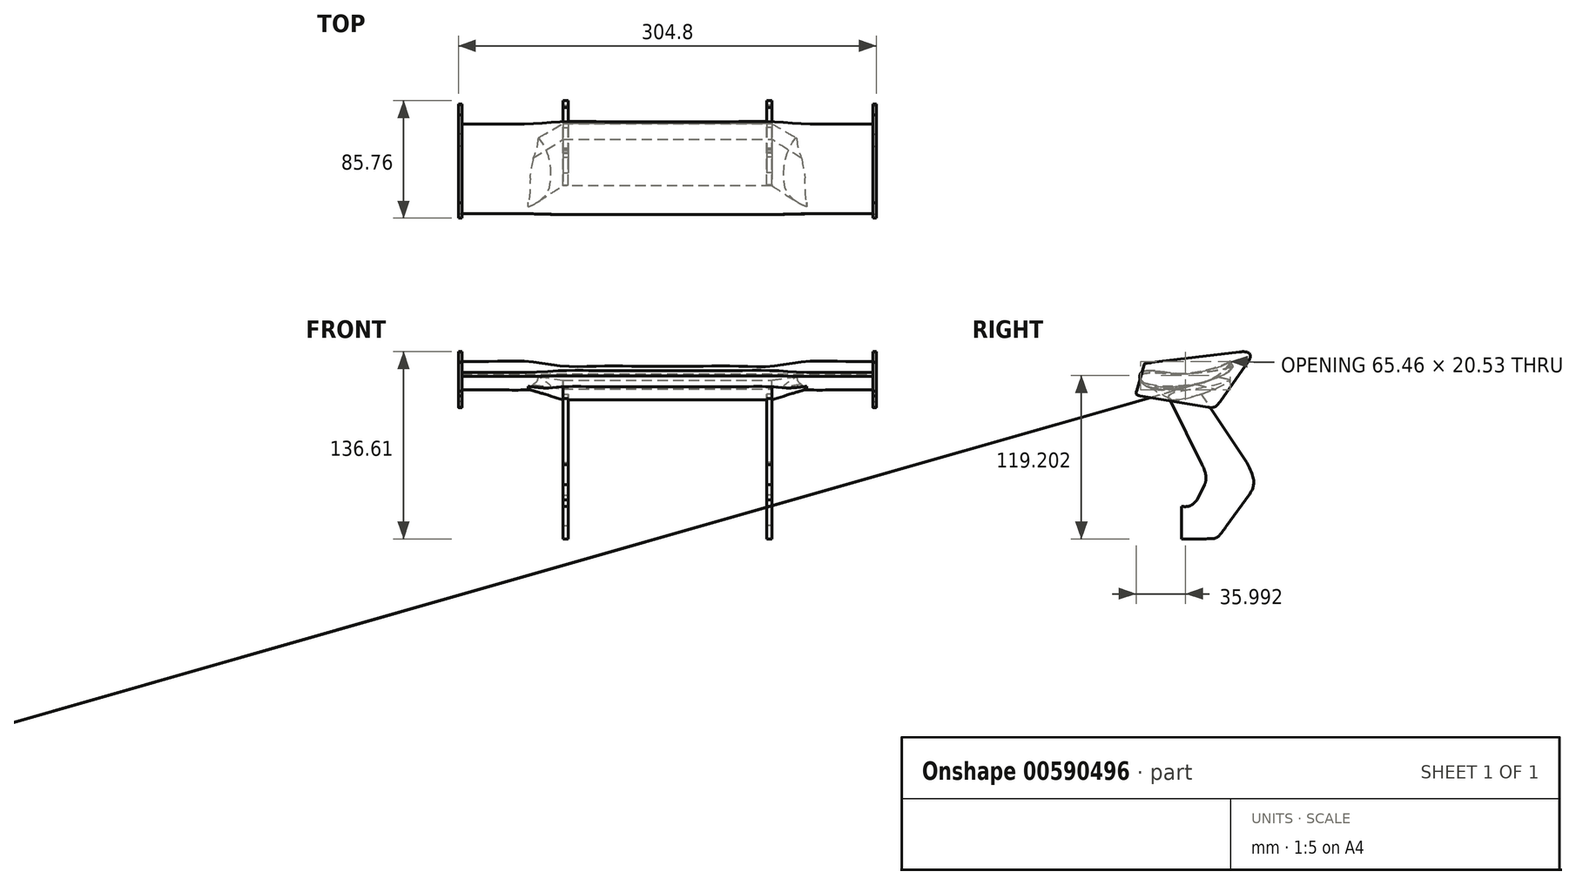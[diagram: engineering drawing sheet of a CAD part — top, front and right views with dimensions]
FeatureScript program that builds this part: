
annotation { "Feature Type Name" : "Feature", "Feature Type Description" : "" }
export const myFeature = defineFeature(function(context is Context, id is Id, definition is map)
    precondition{}
    {
        {
            var Q0;
            Q0=qCreatedBy(makeId("Right.planeOp"),FACE);
            cPlane(context, id + "F0", {"entities" : qUnion([Q0]), "cplaneType" : CPlaneType.OFFSET, "offset" : 25.4 * mm, "width" : 152.4 * mm, "height" : 152.4 * mm});
        }
        {
            var Q0;
            Q0=qCreatedBy(id+"F0.planeOp",FACE);
            cPlane(context, id + "F1", {"entities" : qUnion([Q0]), "cplaneType" : CPlaneType.OFFSET, "offset" : 25.4 * mm, "width" : 152.4 * mm, "height" : 152.4 * mm});
        }
        {
            var Q0;
            Q0=qCreatedBy(id+"F1.planeOp",FACE);
            cPlane(context, id + "F2", {"entities" : qUnion([Q0]), "cplaneType" : CPlaneType.OFFSET, "offset" : 25.4 * mm, "width" : 152.4 * mm, "height" : 152.4 * mm});
        }
        {
            var Q0;
            Q0=qCreatedBy(id+"F2.planeOp",FACE);
            cPlane(context, id + "F3", {"entities" : qUnion([Q0]), "cplaneType" : CPlaneType.OFFSET, "offset" : 25.4 * mm, "width" : 152.4 * mm, "height" : 152.4 * mm});
        }
        {
            var Q0;
            Q0=qCreatedBy(id+"F3.planeOp",FACE);
            cPlane(context, id + "F4", {"entities" : qUnion([Q0]), "cplaneType" : CPlaneType.OFFSET, "offset" : 25.4 * mm, "width" : 152.4 * mm, "height" : 152.4 * mm});
        }
        {
            var Q0;
            Q0=qCreatedBy(id+"F4.planeOp",FACE);
            cPlane(context, id + "F5", {"entities" : qUnion([Q0]), "cplaneType" : CPlaneType.OFFSET, "offset" : 25.4 * mm, "width" : 152.4 * mm, "height" : 152.4 * mm});
        }
        {
            var Q0;
            Q0=qCreatedBy(id+"F0.planeOp",FACE);
            var sketch = newSketch(context, id + "F6", { "sketchPlane" : qUnion([Q0])});
            skFitSpline(sketch, "E0", {"points": [v(-32.84, 0.21) * mm, v(-26.14, -7.71) * mm, v(-13.87, -9.4) * mm, v(5.28, -6.18) * mm, v(19.7, -1.36) * mm, v(29.56, 6.15) * mm, v(32.6, 11.17) * mm], "startDerivative": vector(-17.98, -81.92) * mm, "endDerivative": vector(4.77, 35.61) * mm});
            skFitSpline(sketch, "E1", {"points": [v(32.6, 11.17) * mm, v(14.13, 4.43) * mm, v(-8.08, 1.98) * mm, v(-25.23, 3.12) * mm, v(-32.84, 0.21) * mm], "startDerivative": vector(-30.77, -27.63) * mm, "endDerivative": vector(-5.16, -33) * mm});
            skSolve(sketch);
        }
        {
            var Q0;
            Q0=qCreatedBy(makeId("Right.planeOp"),FACE);
            var sketch = newSketch(context, id + "F7", { "sketchPlane" : qUnion([Q0])});
            skFitSpline(sketch, "E2", {"points": [v(-32.84, 0.21) * mm, v(-26.14, -7.71) * mm, v(-13.87, -9.4) * mm, v(5.28, -6.18) * mm, v(19.7, -1.36) * mm, v(29.56, 6.15) * mm, v(32.6, 11.17) * mm], "startDerivative": vector(-17.98, -81.92) * mm, "endDerivative": vector(4.77, 35.61) * mm});
            skFitSpline(sketch, "E3", {"points": [v(32.6, 11.17) * mm, v(14.13, 4.43) * mm, v(-8.08, 1.98) * mm, v(-25.23, 3.12) * mm, v(-32.84, 0.21) * mm], "startDerivative": vector(-30.77, -27.63) * mm, "endDerivative": vector(-5.16, -33) * mm});
            skSolve(sketch);
        }
        {
            var Q0;
            Q0=qCreatedBy(makeId("Right.planeOp"),FACE);
            cPlane(context, id + "F8", {"entities" : qUnion([Q0]), "cplaneType" : CPlaneType.OFFSET, "offset" : 25.4 * mm, "oppositeDirection" : true, "width" : 152.4 * mm, "height" : 152.4 * mm});
        }
        {
            var Q0;
            Q0=qCreatedBy(id+"F8.planeOp",FACE);
            var sketch = newSketch(context, id + "F9", { "sketchPlane" : qUnion([Q0])});
            skFitSpline(sketch, "E4", {"points": [v(-32.84, 0.21) * mm, v(-26.14, -7.71) * mm, v(-13.87, -9.4) * mm, v(5.28, -6.18) * mm, v(19.7, -1.36) * mm, v(29.56, 6.15) * mm, v(32.6, 11.17) * mm], "startDerivative": vector(-17.98, -81.92) * mm, "endDerivative": vector(4.77, 35.61) * mm});
            skFitSpline(sketch, "E5", {"points": [v(32.6, 11.17) * mm, v(14.13, 4.43) * mm, v(-8.08, 1.98) * mm, v(-25.23, 3.12) * mm, v(-32.84, 0.21) * mm], "startDerivative": vector(-30.77, -27.63) * mm, "endDerivative": vector(-5.16, -33) * mm});
            skSolve(sketch);
        }
        {
            var Q0;
            Q0=qCreatedBy(id+"F4.planeOp",FACE);
            var sketch = newSketch(context, id + "F10", { "sketchPlane" : qUnion([Q0])});
            skFitSpline(sketch, "E6", {"points": [v(-33.46, 0.63) * mm, v(-21.57, -6.7) * mm, v(-14.4, -7.32) * mm, v(5.2, -5.74) * mm, v(19.3, -2.02) * mm, v(30.63, 3.33) * mm, v(34.3, 7.73) * mm], "startDerivative": vector(-17.98, -81.92) * mm, "endDerivative": vector(25.2, 44.48) * mm});
            skFitSpline(sketch, "E7", {"points": [v(34.3, 7.73) * mm, v(13.83, 3.16) * mm, v(-8.88, 2.6) * mm, v(-30.7, 4) * mm, v(-33.46, 0.63) * mm], "startDerivative": vector(-40.26, -20.43) * mm, "endDerivative": vector(-5.16, -33) * mm});
            skSolve(sketch);
        }
        {
            var Q0;
            Q0=qCreatedBy(id+"F3.planeOp",FACE);
            var sketch = newSketch(context, id + "F11", { "sketchPlane" : qUnion([Q0])});
            skFitSpline(sketch, "E8", {"points": [v(-33.46, 0.63) * mm, v(-21.57, -6.7) * mm, v(-14.4, -7.32) * mm, v(5.2, -5.74) * mm, v(19.3, -2.02) * mm, v(30.63, 3.33) * mm, v(34.3, 7.73) * mm], "startDerivative": vector(-17.98, -81.92) * mm, "endDerivative": vector(25.2, 44.48) * mm});
            skFitSpline(sketch, "E9", {"points": [v(34.3, 7.73) * mm, v(13.83, 3.16) * mm, v(-8.88, 2.6) * mm, v(-30.7, 4) * mm, v(-33.46, 0.63) * mm], "startDerivative": vector(-40.26, -20.43) * mm, "endDerivative": vector(-5.16, -33) * mm});
            skSolve(sketch);
        }
        {
            var Q0;
            Q0=qCreatedBy(id+"F2.planeOp",FACE);
            var sketch = newSketch(context, id + "F12", { "sketchPlane" : qUnion([Q0])});
            skFitSpline(sketch, "E10", {"points": [v(-33.46, 0.63) * mm, v(-21.57, -6.7) * mm, v(-14.4, -7.32) * mm, v(5.2, -5.74) * mm, v(19.3, -2.02) * mm, v(30.63, 3.33) * mm, v(34.3, 7.73) * mm], "startDerivative": vector(-17.98, -81.92) * mm, "endDerivative": vector(25.2, 44.48) * mm});
            skFitSpline(sketch, "E11", {"points": [v(34.3, 7.73) * mm, v(13.83, 3.16) * mm, v(-8.88, 2.6) * mm, v(-30.7, 4) * mm, v(-33.46, 0.63) * mm], "startDerivative": vector(-40.26, -20.43) * mm, "endDerivative": vector(-5.16, -33) * mm});
            skSolve(sketch);
        }
        {
            var Q0;
            Q0=qCreatedBy(id+"F1.planeOp",FACE);
            var sketch = newSketch(context, id + "F13", { "sketchPlane" : qUnion([Q0])});
            skFitSpline(sketch, "E12", {"points": [v(-33.46, 0.63) * mm, v(-21.57, -6.7) * mm, v(-14.4, -7.32) * mm, v(5.2, -5.74) * mm, v(19.3, -2.02) * mm, v(30.63, 3.33) * mm, v(34.3, 7.73) * mm], "startDerivative": vector(-17.98, -81.92) * mm, "endDerivative": vector(25.2, 44.48) * mm});
            skFitSpline(sketch, "E13", {"points": [v(34.3, 7.73) * mm, v(13.83, 3.16) * mm, v(-8.88, 2.6) * mm, v(-30.7, 4) * mm, v(-33.46, 0.63) * mm], "startDerivative": vector(-40.26, -20.43) * mm, "endDerivative": vector(-5.16, -33) * mm});
            skSolve(sketch);
        }
        {
            var Q0;
            Q0=qCreatedBy(id+"F4.planeOp",FACE);
            var sketch = newSketch(context, id + "F14", { "sketchPlane" : qUnion([Q0])});
            skFitSpline(sketch, "E14", {"points": [v(32.78, -2.46) * mm, v(15.02, -7.23) * mm, v(-1.74, -10.05) * mm, v(-12.15, -13.46) * mm, v(-11.52, -16.01) * mm, v(-4, -16.68) * mm, v(6.68, -14.11) * mm, v(21.31, -8.94) * mm], "startDerivative": vector(-110.1, -36.5) * mm, "endDerivative": vector(216.78, 82.36) * mm});
            skFitSpline(sketch, "E15", {"points": [v(21.31, -8.94) * mm, v(32.78, -2.46) * mm], "startDerivative": vector(9.03, 3.91) * mm, "endDerivative": vector(0, 2.47) * mm});
            skSolve(sketch);
        }
        {
            var Q0;
            Q0=makeQuery(id+"F14.imprint","IMPRINT",FACE,{"disambiguationData":[TD([[makeQuery(id+"F14.imprint","IMPRINT",EDGE,{"derivedFrom":sQuery(id+"F14.wireOp",EDGE,"E14")}),1.0]])]});
            extrude(context, id + "F15", {"entities" : qUnion([Q0]), "oppositeDirection" : true, "depth" : 76.2 * mm, "offsetDistance" : 25.4 * mm});
        }
        {
            var Q0;
            Q0=qCreatedBy(id+"F0.planeOp",FACE);
            var sketch = newSketch(context, id + "F16", { "sketchPlane" : qUnion([Q0])});
            skFitSpline(sketch, "E16", {"points": [v(18.16, 1.16) * mm, v(-2.89, -2.52) * mm, v(-22.26, -3.13) * mm, v(-28.7, -4.47) * mm, v(-28.03, -6.81) * mm, v(-15.83, -9.03) * mm, v(-8.45, -8.29) * mm, v(5.36, -5) * mm], "startDerivative": vector(-110.1, -36.5) * mm, "endDerivative": vector(240, 68.21) * mm});
            skFitSpline(sketch, "E17", {"points": [v(5.36, -5) * mm, v(18.16, 1.16) * mm], "startDerivative": vector(9.03, 3.91) * mm, "endDerivative": vector(0, 2.47) * mm});
            skSolve(sketch);
        }
        {
            var Q1;
            Q1 = qSketchRegion(id + "F16", true);
            var Q2;
            Q2=makeQuery(id+"F15.opExtrude","CAP_FACE",FACE,{"disambiguationData":[OSD([sQuery(id+"F14.wireOp",EDGE,"E14"),sQuery(id+"F14.wireOp",EDGE,"E15")])],"isStart":false});
            loft(context, id + "F17", {"operationType" : NewBodyOperationType.ADD, "sheetProfilesArray" : [{ "sheetProfileEntities" : qUnion([Q1]) }, { "sheetProfileEntities" : qUnion([Q2]) }]});
        }
        {
            var Q1;
            Q1=makeQuery(id+"F10.imprint","IMPRINT",FACE,{"disambiguationData":[TD([[makeQuery(id+"F10.imprint","IMPRINT",EDGE,{"derivedFrom":sQuery(id+"F10.wireOp",EDGE,"E6")}),1.0]])]});
            var Q2;
            Q2=makeQuery(id+"F11.imprint","IMPRINT",FACE,{"disambiguationData":[TD([[makeQuery(id+"F11.imprint","IMPRINT",EDGE,{"derivedFrom":sQuery(id+"F11.wireOp",EDGE,"E8")}),1.0]])]});
            var Q3;
            Q3=makeQuery(id+"F12.imprint","IMPRINT",FACE,{"disambiguationData":[TD([[makeQuery(id+"F12.imprint","IMPRINT",EDGE,{"derivedFrom":sQuery(id+"F12.wireOp",EDGE,"E10")}),1.0]])]});
            var Q4;
            Q4=makeQuery(id+"F13.imprint","IMPRINT",FACE,{"disambiguationData":[TD([[makeQuery(id+"F13.imprint","IMPRINT",EDGE,{"derivedFrom":sQuery(id+"F13.wireOp",EDGE,"E12")}),1.0]])]});
            var Q5;
            Q5=makeQuery(id+"F6.imprint","IMPRINT",FACE,{"disambiguationData":[TD([[makeQuery(id+"F6.imprint","IMPRINT",EDGE,{"derivedFrom":sQuery(id+"F6.wireOp",EDGE,"E0")}),1.0]])]});
            var Q6;
            Q6=makeQuery(id+"F7.imprint","IMPRINT",FACE,{"disambiguationData":[TD([[makeQuery(id+"F7.imprint","IMPRINT",EDGE,{"derivedFrom":sQuery(id+"F7.wireOp",EDGE,"E2")}),1.0]])]});
            var Q7;
            Q7=makeQuery(id+"F9.imprint","IMPRINT",FACE,{"disambiguationData":[TD([[makeQuery(id+"F9.imprint","IMPRINT",EDGE,{"derivedFrom":sQuery(id+"F9.wireOp",EDGE,"E4")}),1.0]])]});
            loft(context, id + "F18", {"operationType" : NewBodyOperationType.ADD, "sheetProfilesArray" : [{ "sheetProfileEntities" : qUnion([Q1]) }, { "sheetProfileEntities" : qUnion([Q2]) }, { "sheetProfileEntities" : qUnion([Q3]) }, { "sheetProfileEntities" : qUnion([Q4]) }, { "sheetProfileEntities" : qUnion([Q5]) }, { "sheetProfileEntities" : qUnion([Q6]) }, { "sheetProfileEntities" : qUnion([Q7]) }]});
        }
        {
            var Q0;
            Q0=qCreatedBy(id+"F8.planeOp",FACE);
            var sketch = newSketch(context, id + "F19", { "sketchPlane" : qUnion([Q0])});
            skLineSegment(sketch, "E18", {"start": v(-30.46, 8.71) * mm, "end": v(-35.87, -10.4) * mm});
            skLineSegment(sketch, "E19", {"start": v(-24.88, 10.35) * mm, "end": v(39.23, 18.04) * mm});
            skLineSegment(sketch, "E20", {"start": v(45.86, 11.31) * mm, "end": v(25.2, -17.98) * mm});
            skLineSegment(sketch, "E21", {"start": v(16.29, -22.24) * mm, "end": v(-33.2, -13.9) * mm});
            skFitSpline(sketch, "E22", {"points": [v(39.23, 18.04) * mm, v(45.86, 11.31) * mm], "startDerivative": vector(28.72, 3.98) * mm, "endDerivative": vector(-6.83, -10.24) * mm});
            skFitSpline(sketch, "E23", {"points": [v(25.2, -17.98) * mm, v(16.29, -22.24) * mm], "startDerivative": vector(-7.3, -8.45) * mm, "endDerivative": vector(-17.74, 2.75) * mm});
            skFitSpline(sketch, "E24", {"points": [v(-33.2, -13.9) * mm, v(-35.87, -10.4) * mm], "startDerivative": vector(-10.09, 1.57) * mm, "endDerivative": vector(1.24, 5.73) * mm});
            skFitSpline(sketch, "E25", {"points": [v(-30.46, 8.71) * mm, v(-24.88, 10.35) * mm], "startDerivative": vector(0.65, 2.34) * mm, "endDerivative": vector(16.8, 1.68) * mm});
            skSolve(sketch);
        }
        {
            var Q0;
            Q0=makeQuery(id+"F19.imprint","IMPRINT",FACE,{"disambiguationData":[TD([[makeQuery(id+"F19.imprint","IMPRINT",EDGE,{"derivedFrom":sQuery(id+"F19.wireOp",EDGE,"E18")}),1.0]])]});
            extrude(context, id + "F20", {"entities" : qUnion([Q0]), "operationType" : NewBodyOperationType.ADD, "depth" : 2.54 * mm, "offsetDistance" : 25.4 * mm});
        }
        {
            var Q0;
            Q0=qCreatedBy(id+"F2.planeOp",FACE);
            var sketch = newSketch(context, id + "F21", { "sketchPlane" : qUnion([Q0])});
            skLineSegment(sketch, "E26", {"start": v(-12.32, -14.72) * mm, "end": v(11.98, -64.06) * mm});
            skLineSegment(sketch, "E27", {"start": v(10.39, -11.29) * mm, "end": v(44.67, -62.62) * mm});
            skFitSpline(sketch, "E28", {"points": [v(44.67, -62.62) * mm, v(46.26, -86.38) * mm], "startDerivative": vector(23.45, -44.28) * mm, "endDerivative": vector(-9.96, -17.55) * mm});
            skFitSpline(sketch, "E29", {"points": [v(11.98, -64.06) * mm, v(13.74, -78.89) * mm], "startDerivative": vector(13.32, -29.08) * mm, "endDerivative": vector(-2.98, -8.86) * mm});
            skLineSegment(sketch, "E30", {"start": v(13.74, -78.89) * mm, "end": v(8.32, -89.89) * mm});
            skLineSegment(sketch, "E31", {"start": v(46.26, -86.38) * mm, "end": v(30.1, -108.63) * mm});
            skFitSpline(sketch, "E32", {"points": [v(8.32, -89.89) * mm, v(-3.04, -94.66) * mm], "startDerivative": vector(-10.53, -11.5) * mm, "endDerivative": vector(-18.82, 1.91) * mm});
            skFitSpline(sketch, "E33", {"points": [v(30.1, -108.63) * mm, v(13.65, -118.33) * mm], "startDerivative": vector(-23.62, -31.49) * mm, "endDerivative": vector(-30.47, -0.86) * mm});
            skLineSegment(sketch, "E34", {"start": v(13.65, -118.33) * mm, "end": v(-2.94, -118.33) * mm});
            skLineSegment(sketch, "E35", {"start": v(-3.04, -94.66) * mm, "end": v(-2.94, -118.33) * mm});
            skLineSegment(sketch, "E36", {"start": v(-12.32, -14.72) * mm, "end": v(10.39, -11.29) * mm});
            skSolve(sketch);
        }
        {
            var Q0;
            Q0=makeQuery(id+"F21.imprint","IMPRINT",FACE,{"disambiguationData":[TD([[makeQuery(id+"F21.imprint","IMPRINT",EDGE,{"derivedFrom":sQuery(id+"F21.wireOp",EDGE,"E26")}),1.0]])]});
            extrude(context, id + "F22", {"entities" : qUnion([Q0]), "operationType" : NewBodyOperationType.ADD, "oppositeDirection" : true, "depth" : 25.4 * mm, "offsetDistance" : 25.4 * mm, "hasSecondDirection" : true, "secondDirectionOppositeDirection" : true, "secondDirectionDepth" : 21.59 * mm});
        }
        {
            var Q0;
            Q0=makeQuery(id+"F15.opExtrude","SWEPT_BODY",BODY,{"disambiguationData":[OSD([sQuery(id+"F14.wireOp",EDGE,"E14"),sQuery(id+"F14.wireOp",EDGE,"E15")])]});
            var Q1;
            Q1=qCreatedBy(id+"F4.planeOp",FACE);
            mirror(context, id + "F23", {"operationType" : NewBodyOperationType.ADD, "entities" : qUnion([Q0]), "mirrorPlane" : qUnion([Q1])});
        }
    });
